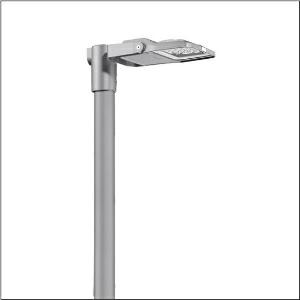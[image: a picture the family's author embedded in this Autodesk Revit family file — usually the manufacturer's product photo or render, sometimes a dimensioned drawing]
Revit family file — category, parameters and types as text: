
# Revit family: floodlight_fl_21_iq_micro___pl61_5xa7762a4c3a_196d
name_source: partatom
category: Lighting Fixtures
units: mm (PartAtom-declared; Revit-internal decimal feet)

## family parameters
Cut with Voids When Loaded = No
Host = Face
Light Source = No
Part Type = Normal
Room Calculation Point = No
Round Connector Dimension = Use Diameter
Shared = No

## types (1)
- --- (1 x LED, 3030 lm, 23.1 W, 4000K)
    Apparent Load = 23 VA
    CIE Flux Codes = 33 65 98 100 100
    Color Rendering = 70
    Color Temperature = 4000K
    Default Elevation = 1800 mm
    Description = Floodlight FL 21 iQ micro, floodlight, primary light control with lens, of PMMA, primary optical cover: protective disc, of toughened safety glass, transparent, light distribution: PL61, light emission: direct distribution, installation type: surface-mounted, lamps: LED, High Power LED, rated values: 3.030lm | 23,1W | 131,2lm/W (begin service life); end service life: 3.030lm | 23,8W; at 50% lumin. flux: 1.515lm | 11W | 137,7lm/W, colour temperature: 4000K, colour rendering: CRI > 70, light colour: 740, light setting 1 begin service life: 100% | 3.030lm | 23,1W | 131,2lm/W | 4.000K, light setting 1 end service life: 23,8W, further light settings possible, control: Auto-Match, Temp-Guard, Night-Set, Smart-Wire, Desk-Remote (wireless, voltage-free reading and setting of iQ features in the workshop via application-optimized NFC function/RFID function), optimised constant luminous flux control (CLO 2.0), Street-Remote, with terminal, 6-pole, mains connection: 220..240V, AC, 50/60Hz, luminaire housing, of diecast aluminium, powder-coated, Siteco® metallic grey (DB 702S), corrosivity category C5 mid according to DIN EN ISO 12944suitable for swimming poolschlorine-resistant, sealing non-destructively replaceable, please order mast flange separately, mast bracket, of steel, galvanised, powder-coated, Siteco® metallic grey (DB 702S), protection rating (complete): IP66, insulation class (complete): insulation class II (safety insulation), certification: CE, ENEC, VDE, protection symbol: D, impact resistance: IK07, permissible operating ambient temperature: -40..+40°C, permissible operating ambient temperature for outdoor applications: -40..+50°C, standard: DIN EN 12944, LABS conformity tested according to VDMA 24364:2018-05, packaging unit: 1 piece

Light Distribution: PL61
    Height = 65 mm
    Lamp = 1 x LED
    Lamp Light Flux = 3030 lm
    Lamp Power = 23.1 W
    Lamp count = 1
    Length = 312 mm
    Luminous efficacy = 131 lm/W
    Manufacturer = Siteco
    ModVariant = No
    Model = 5XA7762A4C3A
    Number of Poles = 1
    OnlyDefault = Yes
    Power Factor = 1
    Product Name = Floodlight FL 21 iQ micro | PL61
    Product group = floodlight | pylon annexe
    ProductGroupID = 6201
    Protection Class = Protection class II
    Protection Degree = IP 66
    RLX_Detail_Level = 1
    RLX_Emergency_Light_Flux = 0 lm
    RLX_Emergency_Type = 0
    RLX_Emergency_Type_DB = No
    RlxData = <blob elided: 102053 chars, md5=126091fd>
    Socket = socket
    Standby Power = 0 W
    System Light Flux = 3030 lm
    System Power = 23 W
    Type Comments = factory setting: luminous flux: 100 % | dim-lin: 254 | 455 mA
    Type Image = l_1007121.jpg
    URL = http://relux.com
    VarID = @adj_195507
    Voltage = 0 V
    Weight = 0.00 kg
    Width = 230 mm

## geometry (parser evidence)
native form markers: Blend x4, Sweep x12
no freeform markers — native parametric forms only
